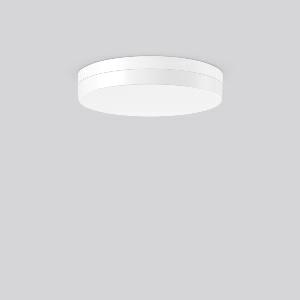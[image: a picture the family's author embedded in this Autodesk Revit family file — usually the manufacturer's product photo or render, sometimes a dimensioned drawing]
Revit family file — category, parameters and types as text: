
# Revit family: flat_slim_round_312632_002_1_730_db53
name_source: partatom
category: Lighting Fixtures
units: mm (PartAtom-declared; Revit-internal decimal feet)

## family parameters
Cut with Voids When Loaded = No
Host = Face
Light Source = No
Part Type = Normal
Room Calculation Point = No
Round Connector Dimension = Use Diameter
Shared = No

## types (1)
- MultiLumen 1 830 (1 x LED Modul 830, 2450 lm, 3000)
    Apparent Load = 18 VA
    CIE Flux Codes = 37 67 88 84 100
    Color Rendering = 80
    Color Temperature = 3000
    Default Elevation = 1800 mm
    Height = 70 mm
    Lamp = 1 x LED Modul 830
    Lamp Light Flux = 2450 lm
    Lamp count = 1
    Length = 400 mm
    Lifetime = 50000 h
    Luminous efficacy = 136 lm/W
    Manufacturer = RZB
    ModVariant = No
    Model = 312632.002.1.730
    Mounting Place = Ceiling
    Mounting Type = Surface mounted
    Number of Poles = 1
    OnlyDefault = Yes
    Power Factor = 1
    Product Name = FLAT SLIM round
    Product group = Surface mounted ceiling and wall luminaires
    ProductGroupID = 305
    Protection Class = Protection class I
    Protection Degree = Degree of protection
    RLX_Detail_Level = 1
    RLX_Emergency_Light_Flux = 0 lm
    RLX_Emergency_Type = 0
    RLX_Emergency_Type_DB = No
    RlxData = <blob elided: 20265 chars, md5=9c7ac1ff>
    Socket = socket
    Standby Power = 0 W
    System Light Flux = 2450 lm
    System Power = 18 W
    Type Comments = MultiLumen 1 830
    Type Image = 312631.002.jpg
    URL = http://relux.com
    VarID = multilumen_1_830
    Voltage = 0 V
    Weight = 0.00 kg
    Width = 0 mm  [stored 0 ft]

note: [stored X ft] marks values corroborated as IEEE doubles in the binary element streams (Revit-internal decimal feet)

## geometry (parser evidence)
native form markers: Blend x4, Sweep x15
no freeform markers — native parametric forms only
